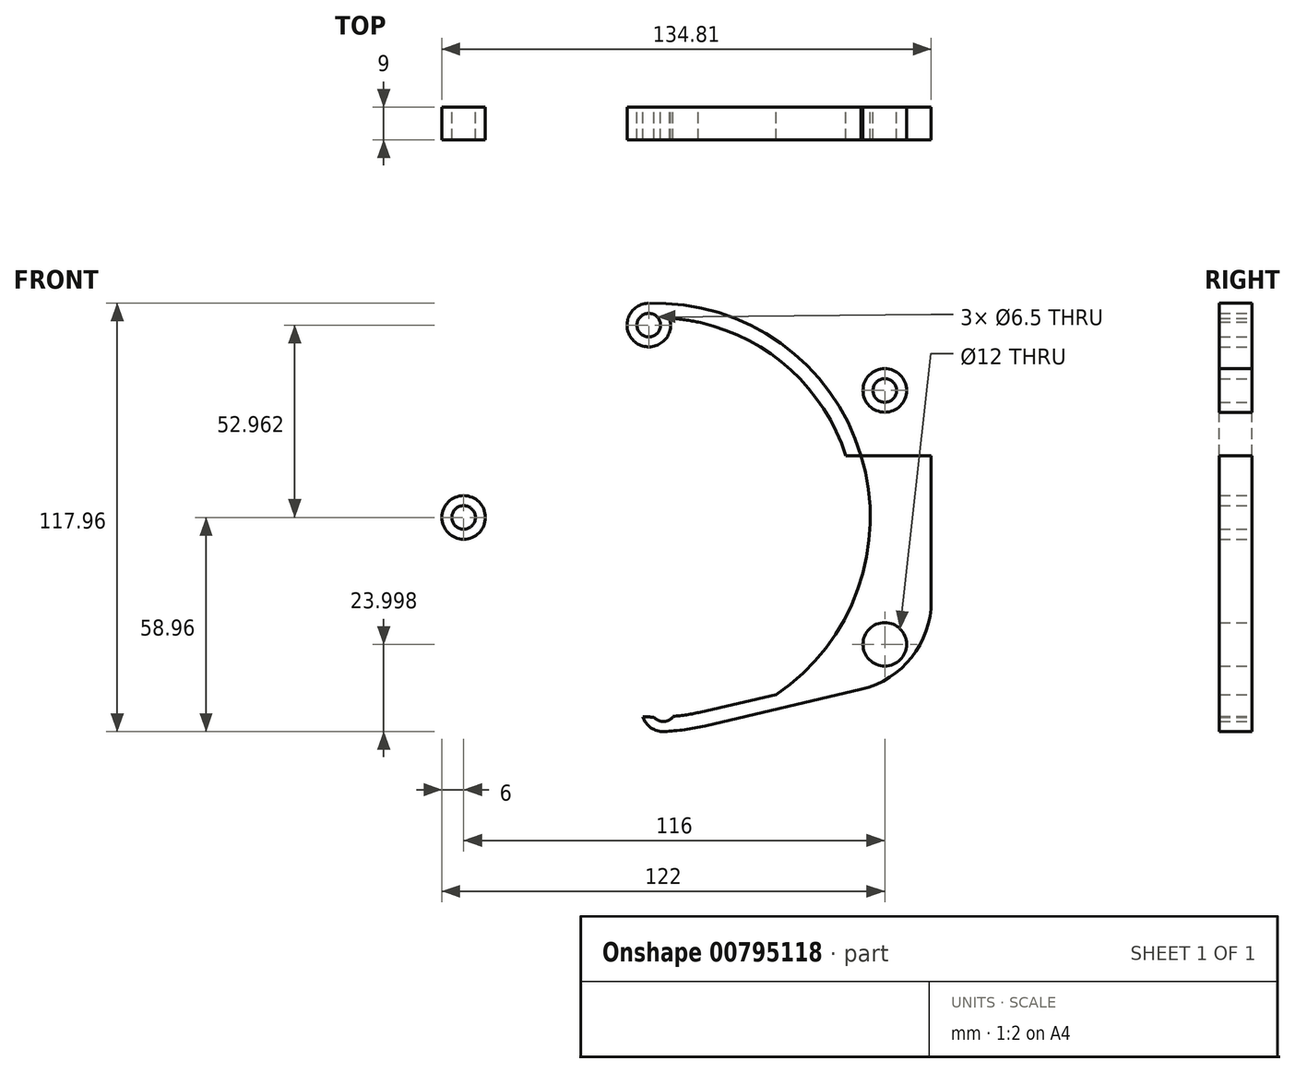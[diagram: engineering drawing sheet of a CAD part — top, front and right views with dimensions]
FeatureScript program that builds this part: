
annotation { "Feature Type Name" : "Feature", "Feature Type Description" : "" }
export const myFeature = defineFeature(function(context is Context, id is Id, definition is map)
    precondition{}
    {
        {
            var Q0;
            Q0=qCreatedBy(makeId("Front.planeOp"),FACE);
            var sketch = newSketch(context, id + "F0", { "sketchPlane" : qUnion([Q0])});
            skCircle(sketch, "E0", {"center": v(0, 0) * mm, "radius": 59 * mm});
            skLineSegment(sketch, "E1", {"start": v(0, 0) * mm, "end": v(165.95, 0) * mm, "construction": true});
            skLineSegment(sketch, "E2", {"start": v(0, 0) * mm, "end": v(0, 108.3) * mm, "construction": true});
            skLineSegment(sketch, "E3.0", {"start": v(0, 42.5) * mm, "end": v(62.49, 42.5) * mm, "construction": true});
            skPoint(sketch, "E4.visualSharp", {"position": v(83, 42.5) * mm});
            skLineSegment(sketch, "E5.MirrorCS", {"start": v(-0.78, -55.08) * mm, "end": v(-0.39, -55) * mm});
            skCircle(sketch, "E6", {"center": v(0, 0) * mm, "radius": 54 * mm, "construction": true});
            skPoint(sketch, "E7.center", {"position": v(0, 0.75) * mm});
            skPoint(sketch, "E8.orphan", {"position": v(-0.78, 55.08) * mm});
            skPoint(sketch, "E9.orphan", {"position": v(83, 21.98) * mm});
            skPoint(sketch, "E10.orphan", {"position": v(79, 22.8) * mm});
            skPoint(sketch, "E11.orphan", {"position": v(62.87, 49.77) * mm});
            skPoint(sketch, "E12.orphan", {"position": v(62.9, 42.42) * mm});
            skPoint(sketch, "E13.visualSharp", {"position": v(71, 40.8) * mm});
            skPoint(sketch, "E14.visualSharp", {"position": v(75, 44.1) * mm});
            skLineSegment(sketch, "E15.0", {"start": v(63, 3.26) * mm, "end": v(63, 111.57) * mm, "construction": true});
            skPoint(sketch, "E16.orphan", {"position": v(58.9, 50.56) * mm});
            skPoint(sketch, "E17.orphan", {"position": v(75, 27.67) * mm});
            skPoint(sketch, "E18.orphan", {"position": v(54.9, 44) * mm});
            skPoint(sketch, "E19.orphan", {"position": v(57.43, 37.35) * mm});
            skLineSegment(sketch, "E20", {"start": v(0, 59) * mm, "end": v(75, 59) * mm, "construction": true});
            skLineSegment(sketch, "E21.0", {"start": v(40, 0) * mm, "end": v(40, 95.27) * mm, "construction": true});
            skLineSegment(sketch, "E22.0", {"start": v(-6.82, 24.67) * mm, "end": v(68.18, 9.76) * mm, "construction": true});
            skLineSegment(sketch, "E23.trimOffspring", {"start": v(62.02, 45.86) * mm, "end": v(63, 45.66) * mm});
            skPoint(sketch, "E24.0.end.orphan", {"position": v(74.8, -0.98) * mm});
            skLineSegment(sketch, "E25.trimOffspring", {"start": v(62.87, 49.77) * mm, "end": v(63, 49.74) * mm});
            skPoint(sketch, "E26.orphan", {"position": v(-53.93, 6.71) * mm});
            skPoint(sketch, "E27.orphan", {"position": v(-53.93, -5.21) * mm});
            skPoint(sketch, "E28.orphan", {"position": v(5.96, -53.18) * mm});
            skPoint(sketch, "E29.orphan", {"position": v(-5.96, -53.18) * mm});
            skPoint(sketch, "E30.start.orphan", {"position": v(74.8, 0.98) * mm});
            skLineSegment(sketch, "E31.MirrorCS", {"start": v(40, 0) * mm, "end": v(40, -95.27) * mm, "construction": true});
            skPoint(sketch, "E32.orphan", {"position": v(74.8, 44.13) * mm});
            skLineSegment(sketch, "E33", {"start": v(0, 0) * mm, "end": v(0, -76.93) * mm, "construction": true});
            skLineSegment(sketch, "E34.0", {"start": v(2, 0) * mm, "end": v(2, -76.93) * mm, "construction": true});
            skCircle(sketch, "E35.0", {"center": v(0, 0) * mm, "radius": 53 * mm, "construction": true});
            skCircle(sketch, "E36", {"center": v(2, -52.96) * mm, "radius": 3.25 * mm});
            skCircle(sketch, "E37", {"center": v(2, -52.96) * mm, "radius": 6 * mm});
            skLineSegment(sketch, "E38.0", {"start": v(-2, 0) * mm, "end": v(-2, 108.3) * mm, "construction": true});
            skCircle(sketch, "E39", {"center": v(-2, 52.96) * mm, "radius": 3.25 * mm});
            skCircle(sketch, "E40", {"center": v(-2, 52.96) * mm, "radius": 6 * mm});
            skLineSegment(sketch, "E41", {"start": v(0, 0) * mm, "end": v(-73.35, 0) * mm, "construction": true});
            skCircle(sketch, "E42", {"center": v(-53, 0) * mm, "radius": 3.25 * mm});
            skCircle(sketch, "E43", {"center": v(-53, 0) * mm, "radius": 6 * mm});
            skLineSegment(sketch, "E44", {"start": v(-2, 52.96) * mm, "end": v(63, 52.96) * mm, "construction": true});
            skLineSegment(sketch, "E45", {"start": v(63, 52.96) * mm, "end": v(63, 34.96) * mm, "construction": true});
            skCircle(sketch, "E46", {"center": v(63, 34.96) * mm, "radius": 3.25 * mm});
            skCircle(sketch, "E47", {"center": v(63, 34.96) * mm, "radius": 6 * mm});
            skCircle(sketch, "E48.MirrorC", {"center": v(63, -34.96) * mm, "radius": 6 * mm});
            skCircle(sketch, "E49.MirrorC", {"center": v(63, -34.96) * mm, "radius": 3.25 * mm});
            skPoint(sketch, "E50.orphan", {"position": v(12.25, -53.62) * mm});
            skArc(sketch, "E51", {"start": v(12.25, -53.62) * mm, "mid": v(55, 0.5) * mm, "end": v(11.28, 53.83) * mm});
            skArc(sketch, "E52", {"start": v(10.72, -53.94) * mm, "mid": v(11.5, -53.79) * mm, "end": v(12.25, -53.62) * mm});
            skLineSegment(sketch, "E53", {"start": v(12.86, -57.58) * mm, "end": v(13.6, -57.4) * mm});
            skArc(sketch, "E54", {"start": v(12.35, -57.7) * mm, "mid": v(-58.67, -6.2) * mm, "end": v(0, 59) * mm});
            skArc(sketch, "E55", {"start": v(13.15, -57.52) * mm, "mid": v(12.75, -57.6) * mm, "end": v(12.35, -57.7) * mm});
            skPoint(sketch, "E56.orphan", {"position": v(12.25, 53.62) * mm});
            skPoint(sketch, "E57.orphan", {"position": v(12.86, 57.58) * mm});
            skLineSegment(sketch, "E58", {"start": v(12.25, 53.62) * mm, "end": v(11.66, 53.75) * mm});
            skArc(sketch, "E59", {"start": v(11.28, 53.83) * mm, "mid": v(-55, 0.28) * mm, "end": v(10.72, -53.94) * mm});
            skLineSegment(sketch, "E60", {"start": v(11.66, 53.75) * mm, "end": v(11.28, 53.83) * mm});
            skLineSegment(sketch, "E61.MirrorCS", {"start": v(52.38, -44.45) * mm, "end": v(11.66, -53.75) * mm});
            skLineSegment(sketch, "E62.MirrorCS", {"start": v(56.52, -47.33) * mm, "end": v(13.15, -57.52) * mm});
            skLineSegment(sketch, "E63", {"start": v(49.7, -48.93) * mm, "end": v(56.38, -47.4) * mm});
            skLineSegment(sketch, "E64", {"start": v(49.76, -45.04) * mm, "end": v(53.38, -44.22) * mm});
            skLineSegment(sketch, "E65", {"start": v(75.8, -19.5) * mm, "end": v(75.8, -23.03) * mm});
            skLineSegment(sketch, "E66", {"start": v(72.8, -19.5) * mm, "end": v(72.8, -19.85) * mm});
            skLineSegment(sketch, "E67.0", {"start": v(71.8, -19.5) * mm, "end": v(71.8, 0.98) * mm});
            skLineSegment(sketch, "E68", {"start": v(75.8, 0.98) * mm, "end": v(75.8, -22.99) * mm});
            skLineSegment(sketch, "E69.0", {"start": v(71.8, 0.98) * mm, "end": v(71.8, -20.08) * mm});
            skArc(sketch, "E70.filletArc", {"start": v(52.38, -44.45) * mm, "mid": v(66.35, -35.66) * mm, "end": v(71.8, -20.08) * mm});
            skArc(sketch, "E71.filletArc", {"start": v(56.52, -47.33) * mm, "mid": v(70.4, -38.51) * mm, "end": v(75.8, -22.99) * mm});
            skLineSegment(sketch, "E72.MirrorCS", {"start": v(52.38, 44.45) * mm, "end": v(11.66, 53.75) * mm});
            skLineSegment(sketch, "E73.MirrorCS", {"start": v(56.52, 47.33) * mm, "end": v(13.15, 57.52) * mm});
            skArc(sketch, "E74.MirrorCS", {"start": v(56.52, 47.33) * mm, "mid": v(70.4, 38.51) * mm, "end": v(75.8, 22.99) * mm});
            skArc(sketch, "E75.MirrorCS", {"start": v(52.38, 44.45) * mm, "mid": v(66.35, 35.66) * mm, "end": v(71.8, 20.08) * mm});
            skLineSegment(sketch, "E76.MirrorCS", {"start": v(71.8, -0.98) * mm, "end": v(71.8, 20.08) * mm});
            skLineSegment(sketch, "E77.MirrorCS", {"start": v(151.61, 0) * mm, "end": v(-14.34, 0) * mm, "construction": true});
            skLineSegment(sketch, "E78.MirrorCS", {"start": v(75.8, -0.98) * mm, "end": v(75.8, 22.99) * mm});
            skLineSegment(sketch, "E79", {"start": v(-59, 0) * mm, "end": v(-59, 17) * mm});
            skLineSegment(sketch, "E80", {"start": v(-59, 17) * mm, "end": v(75.8, 17) * mm});
            skSolve(sketch);
        }
        {
            var Q0;
            {var subQ0=sQuery(id+"F0.wireOp",EDGE,"E40");var subQ1=sQuery(id+"F0.wireOp",EDGE,"E0");var subQ2=makeQuery(id+"F0.imprint","INTERSECT",VERTEX,{"derivedFrom":[subQ1,subQ0]});Q0=makeQuery(id+"F0.imprint","IMPRINT",FACE,{"disambiguationData":[TD([[makeQuery(id+"F0.imprint","IMPRINT",EDGE,{"disambiguationData":[TD([[subQ2,-1.0]])],"derivedFrom":subQ1}),1.0]])]});}
            var Q1;
            {var subQ0=sQuery(id+"F0.wireOp",EDGE,"E43");var subQ1=sQuery(id+"F0.wireOp",EDGE,"E0");var subQ2=makeQuery(id+"F0.imprint","INTERSECT",VERTEX,{"derivedFrom":[subQ1,subQ0]});Q1=makeQuery(id+"F0.imprint","IMPRINT",FACE,{"disambiguationData":[TD([[makeQuery(id+"F0.imprint","IMPRINT",EDGE,{"disambiguationData":[TD([[subQ2,-1.0]])],"derivedFrom":subQ1}),1.0]])]});}
            var Q2;
            {var subQ3=sQuery(id+"F0.wireOp",EDGE,"E0");var subQ8=makeQuery(id+"F0.imprint","INTERSECT",VERTEX,{"derivedFrom":[subQ3,sQuery(id+"F0.wireOp",EDGE,"2vaRvR2S-pXXS-RNvG-eToD-BuaRcgSiFItB")]});Q2=makeQuery(id+"F0.imprint","IMPRINT",FACE,{"disambiguationData":[TD([[makeQuery(id+"F0.imprint","IMPRINT",EDGE,{"disambiguationData":[TD([[subQ8,1.0]])],"derivedFrom":subQ3}),1.0]])]});}
            var Q3;
            {var subQ8=sQuery(id+"F0.wireOp",EDGE,"E52");Q3=makeQuery(id+"F0.imprint","IMPRINT",FACE,{"disambiguationData":[TD([[makeQuery(id+"F0.imprint","IMPRINT",EDGE,{"derivedFrom":subQ8}),-1.0]])]});}
            var Q4;
            {var subQ0=sQuery(id+"F0.wireOp",EDGE,"E51");var subQ1=sQuery(id+"F0.wireOp",EDGE,"E39");var subQ2=makeQuery(id+"F0.imprint","INTERSECT",VERTEX,{"disambiguationData":[OD(0.0)],"derivedFrom":[subQ1,subQ0]});Q4=makeQuery(id+"F0.imprint","IMPRINT",FACE,{"disambiguationData":[TD([[makeQuery(id+"F0.imprint","IMPRINT",EDGE,{"disambiguationData":[TD([[subQ2,-1.0]])],"derivedFrom":subQ1}),-1.0]])]});}
            var Q5;
            {var subQ0=sQuery(id+"F0.wireOp",EDGE,"E51");var subQ1=sQuery(id+"F0.wireOp",EDGE,"E42");var subQ2=makeQuery(id+"F0.imprint","INTERSECT",VERTEX,{"disambiguationData":[OD(0.0)],"derivedFrom":[subQ1,subQ0]});Q5=makeQuery(id+"F0.imprint","IMPRINT",FACE,{"disambiguationData":[TD([[makeQuery(id+"F0.imprint","IMPRINT",EDGE,{"disambiguationData":[TD([[subQ2,-1.0]])],"derivedFrom":subQ1}),-1.0]])]});}
            var Q6;
            {var subQ4=sQuery(id+"F0.wireOp",EDGE,"E36");var subQ7=makeQuery(id+"F0.imprint","INTERSECT",VERTEX,{"derivedFrom":[sQuery(id+"F0.wireOp",EDGE,"E5.MirrorCS"),subQ4]});Q6=makeQuery(id+"F0.imprint","IMPRINT",FACE,{"disambiguationData":[TD([[makeQuery(id+"F0.imprint","IMPRINT",EDGE,{"disambiguationData":[TD([[subQ7,1.0]])],"derivedFrom":subQ4}),-1.0]])]});}
            var Q7;
            {var subQ0=sQuery(id+"F0.wireOp",EDGE,"E47");var subQ1=sQuery(id+"F0.wireOp",EDGE,"3c09c76e-d93d-49e4-8b07-af30fd3a254a");var subQ2=makeQuery(id+"F0.imprint","INTERSECT",VERTEX,{"disambiguationData":[OD(0.0)],"derivedFrom":[subQ1,subQ0]});Q7=makeQuery(id+"F0.imprint","IMPRINT",FACE,{"disambiguationData":[TD([[makeQuery(id+"F0.imprint","IMPRINT",EDGE,{"disambiguationData":[TD([[subQ2,-1.0]])],"derivedFrom":subQ1}),-1.0]])]});}
            var Q8;
            {var subQ0=sQuery(id+"F0.wireOp",EDGE,"E47");var subQ1=sQuery(id+"F0.wireOp",EDGE,"3c09c76e-d93d-49e4-8b07-af30fd3a254a");var subQ2=makeQuery(id+"F0.imprint","INTERSECT",VERTEX,{"disambiguationData":[OD(0.0)],"derivedFrom":[subQ1,subQ0]});Q8=makeQuery(id+"F0.imprint","IMPRINT",FACE,{"disambiguationData":[TD([[makeQuery(id+"F0.imprint","IMPRINT",EDGE,{"disambiguationData":[TD([[subQ2,-1.0]])],"derivedFrom":subQ1}),1.0]])]});}
            var Q9;
            {var subQ0=sQuery(id+"F0.wireOp",EDGE,"d6201248-584e-4a8c-bb37-031c3e83135e0.MirrorCS");var subQ1=sQuery(id+"F0.wireOp",EDGE,"E48.MirrorC");var subQ2=makeQuery(id+"F0.imprint","INTERSECT",VERTEX,{"disambiguationData":[OD(0.0)],"derivedFrom":[subQ1,subQ0]});Q9=makeQuery(id+"F0.imprint","IMPRINT",FACE,{"disambiguationData":[TD([[makeQuery(id+"F0.imprint","IMPRINT",EDGE,{"disambiguationData":[TD([[subQ2,-1.0]])],"derivedFrom":subQ1}),-1.0]])]});}
            var Q10;
            {var subQ0=sQuery(id+"F0.wireOp",EDGE,"d6201248-584e-4a8c-bb37-031c3e83135e0.MirrorCS");var subQ1=sQuery(id+"F0.wireOp",EDGE,"E48.MirrorC");var subQ2=makeQuery(id+"F0.imprint","INTERSECT",VERTEX,{"disambiguationData":[OD(0.0)],"derivedFrom":[subQ1,subQ0]});Q10=makeQuery(id+"F0.imprint","IMPRINT",FACE,{"disambiguationData":[TD([[makeQuery(id+"F0.imprint","IMPRINT",EDGE,{"disambiguationData":[TD([[subQ2,1.0]])],"derivedFrom":subQ1}),-1.0]])]});}
            var Q11;
            {var subQ0=sQuery(id+"F0.wireOp",EDGE,"39bf92b3-4eb5-4492-95c3-396b1ac7ee7b.0");var subQ1=sQuery(id+"F0.wireOp",EDGE,"E0");var subQ2=makeQuery(id+"F0.imprint","INTERSECT",VERTEX,{"derivedFrom":[subQ1,subQ0]});Q11=makeQuery(id+"F0.imprint","IMPRINT",FACE,{"disambiguationData":[TD([[makeQuery(id+"F0.imprint","IMPRINT",EDGE,{"disambiguationData":[TD([[subQ2,1.0]])],"derivedFrom":subQ1}),1.0]])]});}
            var Q12;
            {var subQ0=sQuery(id+"F0.wireOp",EDGE,"46ceafde-2f06-46b5-9eb1-3f2648746f5f0.MirrorCS");var subQ1=sQuery(id+"F0.wireOp",EDGE,"E0");var subQ2=makeQuery(id+"F0.imprint","INTERSECT",VERTEX,{"derivedFrom":[subQ1,subQ0]});Q12=makeQuery(id+"F0.imprint","IMPRINT",FACE,{"disambiguationData":[TD([[makeQuery(id+"F0.imprint","IMPRINT",EDGE,{"disambiguationData":[TD([[subQ2,1.0]])],"derivedFrom":subQ1}),1.0]])]});}
            var Q13;
            {var subQ0=sQuery(id+"F0.wireOp",EDGE,"E58");Q13=makeQuery(id+"F0.imprint","IMPRINT",FACE,{"disambiguationData":[TD([[makeQuery(id+"F0.imprint","IMPRINT",EDGE,{"derivedFrom":subQ0}),-1.0]])]});}
            var Q14;
            {var subQ0=sQuery(id+"F0.wireOp",EDGE,"f32c06ff-43e2-4377-a352-c315e3dc1a05.2");var subQ1=sQuery(id+"F0.wireOp",EDGE,"E0");var subQ2=makeQuery(id+"F0.imprint","INTERSECT",VERTEX,{"derivedFrom":[subQ1,subQ0]});Q14=makeQuery(id+"F0.imprint","IMPRINT",FACE,{"disambiguationData":[TD([[makeQuery(id+"F0.imprint","IMPRINT",EDGE,{"disambiguationData":[TD([[subQ2,1.0]])],"derivedFrom":subQ1}),1.0]])]});}
            var Q15;
            {var subQ0=sQuery(id+"F0.wireOp",EDGE,"E60");Q15=makeQuery(id+"F0.imprint","IMPRINT",FACE,{"disambiguationData":[TD([[makeQuery(id+"F0.imprint","IMPRINT",EDGE,{"derivedFrom":subQ0}),-1.0]])]});}
            var Q16;
            {var subQ0=sQuery(id+"F0.wireOp",EDGE,"69b04a04-3b2d-4d58-8972-252a60eb653b0.MirrorCS");var subQ1=sQuery(id+"F0.wireOp",EDGE,"E0");var subQ2=makeQuery(id+"F0.imprint","INTERSECT",VERTEX,{"derivedFrom":[subQ1,subQ0]});Q16=makeQuery(id+"F0.imprint","IMPRINT",FACE,{"disambiguationData":[TD([[makeQuery(id+"F0.imprint","IMPRINT",EDGE,{"disambiguationData":[TD([[subQ2,1.0]])],"derivedFrom":subQ1}),1.0]])]});}
            var Q17;
            Q17=makeQuery(id+"F0.imprint","IMPRINT",FACE,{"disambiguationData":[TD([[makeQuery(id+"F0.imprint","IMPRINT",EDGE,{"derivedFrom":sQuery(id+"F0.wireOp",EDGE,"E46")}),-1.0]])]});
            var Q18;
            {var subQ0=sQuery(id+"F0.wireOp",EDGE,"f5c17f76-5a54-4f40-a94d-2cc8b76ceb550.MirrorCS");var subQ1=sQuery(id+"F0.wireOp",EDGE,"E47");var subQ2=makeQuery(id+"F0.imprint","INTERSECT",VERTEX,{"disambiguationData":[OD(0.0)],"derivedFrom":[subQ1,subQ0]});Q18=makeQuery(id+"F0.imprint","IMPRINT",FACE,{"disambiguationData":[TD([[makeQuery(id+"F0.imprint","IMPRINT",EDGE,{"disambiguationData":[TD([[subQ2,1.0]])],"derivedFrom":subQ1}),1.0]])]});}
            var Q19;
            {var subQ14=sQuery(id+"F0.wireOp",EDGE,"E74.MirrorCS");Q19=makeQuery(id+"F0.imprint","IMPRINT",FACE,{"disambiguationData":[TD([[makeQuery(id+"F0.imprint","IMPRINT",EDGE,{"derivedFrom":subQ14}),-1.0]])]});}
            var Q20;
            {var subQ0=sQuery(id+"F0.wireOp",EDGE,"E72.MirrorCS");var subQ1=sQuery(id+"F0.wireOp",EDGE,"E0");var subQ2=makeQuery(id+"F0.imprint","INTERSECT",VERTEX,{"derivedFrom":[subQ1,subQ0]});Q20=makeQuery(id+"F0.imprint","IMPRINT",FACE,{"disambiguationData":[TD([[makeQuery(id+"F0.imprint","IMPRINT",EDGE,{"disambiguationData":[TD([[subQ2,1.0]])],"derivedFrom":subQ1}),1.0]])]});}
            var Q21;
            {var subQ0=sQuery(id+"F0.wireOp",EDGE,"E59");var subQ1=sQuery(id+"F0.wireOp",EDGE,"E39");var subQ2=makeQuery(id+"F0.imprint","INTERSECT",VERTEX,{"disambiguationData":[OD(0.0)],"derivedFrom":[subQ1,subQ0]});Q21=makeQuery(id+"F0.imprint","IMPRINT",FACE,{"disambiguationData":[TD([[makeQuery(id+"F0.imprint","IMPRINT",EDGE,{"disambiguationData":[TD([[subQ2,1.0]])],"derivedFrom":subQ1}),-1.0]])]});}
            var Q22;
            {var subQ0=sQuery(id+"F0.wireOp",EDGE,"E59");var subQ1=sQuery(id+"F0.wireOp",EDGE,"E36");var subQ2=makeQuery(id+"F0.imprint","INTERSECT",VERTEX,{"disambiguationData":[OD(0.0)],"derivedFrom":[subQ1,subQ0]});Q22=makeQuery(id+"F0.imprint","IMPRINT",FACE,{"disambiguationData":[TD([[makeQuery(id+"F0.imprint","IMPRINT",EDGE,{"disambiguationData":[TD([[subQ2,1.0]])],"derivedFrom":subQ1}),-1.0]])]});}
            var Q23;
            {var subQ0=sQuery(id+"F0.wireOp",EDGE,"E59");var subQ1=sQuery(id+"F0.wireOp",EDGE,"E42");var subQ2=makeQuery(id+"F0.imprint","INTERSECT",VERTEX,{"disambiguationData":[OD(0.0)],"derivedFrom":[subQ1,subQ0]});Q23=makeQuery(id+"F0.imprint","IMPRINT",FACE,{"disambiguationData":[TD([[makeQuery(id+"F0.imprint","IMPRINT",EDGE,{"disambiguationData":[TD([[subQ2,1.0]])],"derivedFrom":subQ1}),-1.0]])]});}
            extrude(context, id + "F1", {"entities" : qUnion([Q0, Q1, Q2, Q3, Q4, Q5, Q6, Q7, Q8, Q9, Q10, Q11, Q12, Q13, Q14, Q15, Q16, Q17, Q18, Q19, Q20, Q21, Q22, Q23]), "depth" : 9 * mm, "offsetDistance" : 25 * mm});
        }
    });
